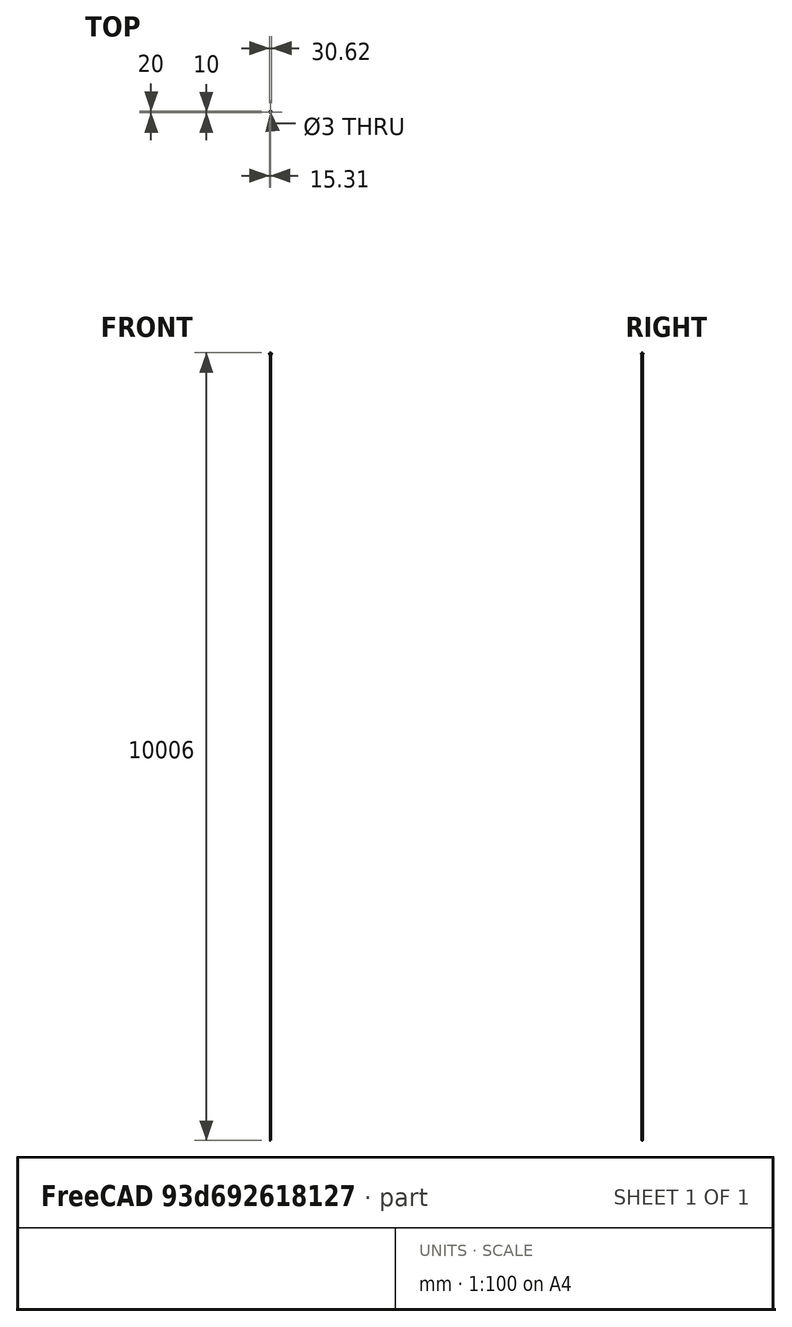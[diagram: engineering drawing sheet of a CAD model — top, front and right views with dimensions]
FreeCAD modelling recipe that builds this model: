
FCSTD DOCUMENT  (FreeCAD 0.16R)
Label: KetchupA1
License: All rights reserved
LicenseURL: http://en.wikipedia.org/wiki/All_rights_reserved
objects: Sketcher::SketchObject×5, PartDesign::Pocket×3, PartDesign::Fillet×3, Part::Cut×2, PartDesign::Pad×1, PartDesign::Revolution×1, Part::Sphere×1, Part::Box×1, Mesh::Feature×1
note: 22 computed .brp shape members not serialized (recipe doc carries the construction recipe); baked Part::Feature solids carry a one-line shape summary decoded from their .brp

FEATURE [Sketcher::SketchObject] Sketch
  sketch-geometry (4):
    g0: LineSegment StartX=-3.625 StartY=3.625 StartZ=0 EndX=3.625 EndY=3.625 EndZ=0
    g1: LineSegment StartX=3.625 StartY=3.625 StartZ=0 EndX=3.625 EndY=-3.625 EndZ=0
    g2: LineSegment StartX=3.625 StartY=-3.625 StartZ=0 EndX=-3.625 EndY=-3.625 EndZ=0
    g3: LineSegment StartX=-3.625 StartY=-3.625 StartZ=0 EndX=-3.625 EndY=3.625 EndZ=0
  constraints (11):
    c: Coincident(g0,g1)
    c: Coincident(g1,g2)
    c: Coincident(g2,g3)
    c: Coincident(g3,g0)
    c: Horizontal(g0)
    c: Horizontal(g2)
    c: Vertical(g1)
    c: Vertical(g3)
    c: Symmetric(g1,g0,g-1)
    c: Equal(g1,g0)
    c: Distance(g1) = 7.25
FEATURE [PartDesign::Pad] Pad
  Length = 16
  Length2 = 100
  Sketch = -> Sketch
  Type = 0
FEATURE [Sketcher::SketchObject] Sketch003
  Placement = pos=(0,0,16) rot=(0,0,1;0rad)
  Support = -> Pad [Face6]
  sketch-geometry (2):
    g0: ArcOfCircle CenterX=0 CenterY=0 CenterZ=0 NormalX=0 NormalY=0 NormalZ=1 Radius=10 StartAngle=0 EndAngle=3.14159
    g1: LineSegment StartX=-10 StartY=0 StartZ=0 EndX=10 EndY=0 EndZ=0
  constraints (6):
    c: Coincident(g0,g-1)
    c: PointOnObject(g0,g-1)
    c: PointOnObject(g0,g-1)
    c: Radius(g0) = 10
    c: Coincident(g1,g0)
    c: Coincident(g1,g0)
FEATURE [PartDesign::Revolution] Revolution
  Angle = 360
  Axis = (1,0,0)
  Base = (0,0,16)
  ReferenceAxis = -> Sketch003 [H_Axis]
  Reversed = true
  Sketch = -> Sketch003
FEATURE [Part::Sphere] Sphere
  Angle1 = -90
  Angle2 = 90
  Angle3 = 360
  Placement = pos=(0,0,15) rot=(0,0,1;0rad)
  Radius = 8.5
FEATURE [Part::Cut] Cut
  Base = -> Revolution
  Tool = -> Sphere
FEATURE [Part::Box] Box  label="Cube"
  Height = 30
  Length = 30
  Placement = pos=(-15,-15,20) rot=(0,0,1;0rad)
  Width = 30
FEATURE [Part::Cut] Cut001
  Base = -> Cut
  Tool = -> Box
FEATURE [Sketcher::SketchObject] Sketch006
  Placement = pos=(0,0,20) rot=(0,0,1;0rad)
  Support = -> Cut001 [Face7]
  sketch-geometry (1):
    g0: Circle CenterX=0 CenterY=0 CenterZ=0 NormalX=0 NormalY=0 NormalZ=1 Radius=1.5
  constraints (2):
    c: Radius(g0) = 1.5
    c: Coincident(g0,g-1)
FEATURE [PartDesign::Pocket] Pocket
  Length = 5
  Sketch = -> Sketch006
  Type = 1
FEATURE [Sketcher::SketchObject] Sketch005
  Placement = pos=(0,0,20) rot=(0,0,1;0rad)
  Support = -> Pocket [Face9]
  sketch-geometry (4):
    g0: LineSegment StartX=-15.3059 StartY=0.75 StartZ=0 EndX=15.3059 EndY=0.75 EndZ=0
    g1: LineSegment StartX=15.3059 StartY=0.75 StartZ=0 EndX=15.3059 EndY=-0.75 EndZ=0
    g2: LineSegment StartX=15.3059 StartY=-0.75 StartZ=0 EndX=-15.3059 EndY=-0.75 EndZ=0
    g3: LineSegment StartX=-15.3059 StartY=-0.75 StartZ=0 EndX=-15.3059 EndY=0.75 EndZ=0
  constraints (10):
    c: Coincident(g0,g1)
    c: Coincident(g1,g2)
    c: Coincident(g2,g3)
    c: Coincident(g3,g0)
    c: Horizontal(g0)
    c: Horizontal(g2)
    c: Vertical(g1)
    c: Vertical(g3)
    c: Symmetric(g1,g0,g-1)
    c: Distance(g1) = 1.5
FEATURE [PartDesign::Pocket] Pocket001
  Length = 5
  Sketch = -> Sketch005
  Type = 0
FEATURE [Sketcher::SketchObject] Sketch004
  Placement = pos=(0,0,20) rot=(0,0,1;0rad)
  Support = -> Pocket001 [Face17]
  sketch-geometry (4):
    g0: LineSegment StartX=-0.75 StartY=13.7981 StartZ=0 EndX=0.75 EndY=13.7981 EndZ=0
    g1: LineSegment StartX=0.75 StartY=13.7981 StartZ=0 EndX=0.75 EndY=-13.7981 EndZ=0
    g2: LineSegment StartX=0.75 StartY=-13.7981 StartZ=0 EndX=-0.75 EndY=-13.7981 EndZ=0
    g3: LineSegment StartX=-0.75 StartY=-13.7981 StartZ=0 EndX=-0.75 EndY=13.7981 EndZ=0
  constraints (11):
    c: Coincident(g0,g1)
    c: Coincident(g1,g2)
    c: Coincident(g2,g3)
    c: Coincident(g3,g0)
    c: Horizontal(g0)
    c: Horizontal(g2)
    c: Vertical(g1)
    c: Vertical(g3)
    c: Symmetric(g1,g2,g-2)
    c: Distance(g0) = 1.5
    c: Symmetric(g1,g0,g-1)
FEATURE [PartDesign::Pocket] Pocket002
  Length = 5
  Sketch = -> Sketch004
  Type = 0
FEATURE [PartDesign::Fillet] Fillet
  Base = -> Pocket002 [Edge39,Edge35,Edge47,Edge43,Edge71,Edge19,Edge23,Edge64,Edge67,Edge68,Edge53,Edge60,Edge51,Edge57,Edge61,Edge56]
  Radius = 0.29
FEATURE [PartDesign::Fillet] Fillet001
  Base = -> Fillet [Edge28,Edge26,Edge25,Edge27]
  Radius = 5
FEATURE [PartDesign::Fillet] Fillet002
  Base = -> Fillet001 [Edge112,Edge108,Edge109,Edge106]
  Radius = 0.2
FEATURE [Mesh::Feature] Mesh  label="Fillet002 (Meshed)"
